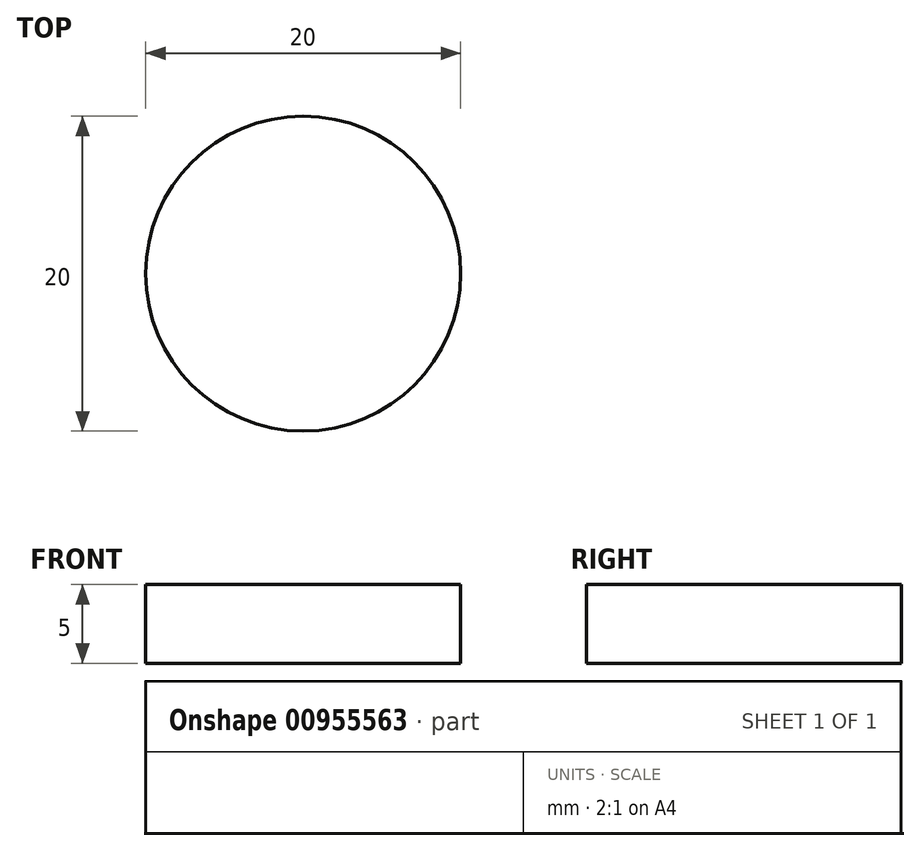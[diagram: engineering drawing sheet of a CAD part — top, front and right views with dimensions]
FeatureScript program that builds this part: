
annotation { "Feature Type Name" : "Feature", "Feature Type Description" : "" }
export const myFeature = defineFeature(function(context is Context, id is Id, definition is map)
    precondition{}
    {
        {
            var Q0;
            Q0=qCreatedBy(makeId("Top.planeOp"),FACE);
            var sketch = newSketch(context, id + "F0", { "sketchPlane" : qUnion([Q0])});
            skCircle(sketch, "E0", {"center": v(0, 0) * mm, "radius": 95 * mm});
            skCircle(sketch, "E1", {"center": v(0, 0) * mm, "radius": 10 * mm});
            skCircle(sketch, "E2", {"center": v(0, 0) * mm, "radius": 20 * mm});
            skCircle(sketch, "E3", {"center": v(0, 0) * mm, "radius": 35 * mm});
            skCircle(sketch, "E4", {"center": v(0, 0) * mm, "radius": 50 * mm});
            skCircle(sketch, "E5", {"center": v(0, 0) * mm, "radius": 65 * mm});
            skCircle(sketch, "E6", {"center": v(0, 0) * mm, "radius": 80 * mm});
            skLineSegment(sketch, "E7", {"start": v(0, 0) * mm, "end": v(0, 95) * mm});
            skLineSegment(sketch, "E8", {"start": v(24.75, 24.75) * mm, "end": v(67.18, 67.18) * mm});
            skLineSegment(sketch, "E9", {"start": v(19.13, 46.2) * mm, "end": v(36.35, 87.77) * mm});
            skLineSegment(sketch, "E10", {"start": v(12.68, 63.75) * mm, "end": v(18.53, 93.17) * mm});
            skLineSegment(sketch, "E11", {"start": v(7.84, 79.61) * mm, "end": v(9.31, 94.54) * mm});
            skLineSegment(sketch, "E12.1.0", {"start": v(-24.75, 24.75) * mm, "end": v(-67.18, 67.18) * mm});
            skLineSegment(sketch, "E12.2.0", {"start": v(-24.75, -24.75) * mm, "end": v(-67.18, -67.18) * mm});
            skLineSegment(sketch, "E12.3.0", {"start": v(24.75, -24.75) * mm, "end": v(67.18, -67.18) * mm});
            skLineSegment(sketch, "E13.1.0", {"start": v(-19.13, 46.2) * mm, "end": v(-36.35, 87.77) * mm});
            skLineSegment(sketch, "E13.2.0", {"start": v(-46.2, 19.13) * mm, "end": v(-87.77, 36.35) * mm});
            skLineSegment(sketch, "E13.3.0", {"start": v(-46.2, -19.13) * mm, "end": v(-87.77, -36.35) * mm});
            skLineSegment(sketch, "E13.4.0", {"start": v(-19.13, -46.2) * mm, "end": v(-36.35, -87.77) * mm});
            skLineSegment(sketch, "E13.5.0", {"start": v(19.13, -46.2) * mm, "end": v(36.35, -87.77) * mm});
            skLineSegment(sketch, "E13.6.0", {"start": v(46.2, -19.13) * mm, "end": v(87.77, -36.35) * mm});
            skLineSegment(sketch, "E13.7.0", {"start": v(46.2, 19.13) * mm, "end": v(87.77, 36.35) * mm});
            skLineSegment(sketch, "E14.1.0", {"start": v(-12.68, 63.75) * mm, "end": v(-18.53, 93.17) * mm});
            skLineSegment(sketch, "E14.2.0", {"start": v(-36.11, 54.05) * mm, "end": v(-52.78, 78.99) * mm});
            skLineSegment(sketch, "E14.3.0", {"start": v(-54.05, 36.11) * mm, "end": v(-78.99, 52.78) * mm});
            skLineSegment(sketch, "E14.4.0", {"start": v(-63.75, 12.68) * mm, "end": v(-93.17, 18.53) * mm});
            skLineSegment(sketch, "E14.5.0", {"start": v(-63.75, -12.68) * mm, "end": v(-93.17, -18.53) * mm});
            skLineSegment(sketch, "E14.6.0", {"start": v(-54.05, -36.11) * mm, "end": v(-78.99, -52.78) * mm});
            skLineSegment(sketch, "E14.7.0", {"start": v(-36.11, -54.05) * mm, "end": v(-52.78, -78.99) * mm});
            skLineSegment(sketch, "E14.8.0", {"start": v(-12.68, -63.75) * mm, "end": v(-18.53, -93.17) * mm});
            skLineSegment(sketch, "E14.9.0", {"start": v(12.68, -63.75) * mm, "end": v(18.53, -93.17) * mm});
            skLineSegment(sketch, "E14.10.0", {"start": v(36.11, -54.05) * mm, "end": v(52.78, -78.99) * mm});
            skLineSegment(sketch, "E14.11.0", {"start": v(54.05, -36.11) * mm, "end": v(78.99, -52.78) * mm});
            skLineSegment(sketch, "E14.12.0", {"start": v(63.75, -12.68) * mm, "end": v(93.17, -18.53) * mm});
            skLineSegment(sketch, "E14.13.0", {"start": v(63.75, 12.68) * mm, "end": v(93.17, 18.53) * mm});
            skLineSegment(sketch, "E14.14.0", {"start": v(54.05, 36.11) * mm, "end": v(78.99, 52.78) * mm});
            skLineSegment(sketch, "E14.15.0", {"start": v(36.11, 54.05) * mm, "end": v(52.78, 78.99) * mm});
            skLineSegment(sketch, "E15.1.0", {"start": v(-7.84, 79.61) * mm, "end": v(-9.31, 94.54) * mm});
            skLineSegment(sketch, "E15.2.0", {"start": v(-23.22, 76.56) * mm, "end": v(-27.58, 90.9) * mm});
            skLineSegment(sketch, "E15.3.0", {"start": v(-37.71, 70.55) * mm, "end": v(-44.78, 83.78) * mm});
            skLineSegment(sketch, "E15.4.0", {"start": v(-50.75, 61.84) * mm, "end": v(-60.27, 73.44) * mm});
            skLineSegment(sketch, "E15.5.0", {"start": v(-61.84, 50.75) * mm, "end": v(-73.44, 60.27) * mm});
            skLineSegment(sketch, "E15.6.0", {"start": v(-70.55, 37.71) * mm, "end": v(-83.78, 44.78) * mm});
            skLineSegment(sketch, "E15.7.0", {"start": v(-76.56, 23.22) * mm, "end": v(-90.9, 27.58) * mm});
            skLineSegment(sketch, "E15.8.0", {"start": v(-79.61, 7.84) * mm, "end": v(-94.54, 9.31) * mm});
            skLineSegment(sketch, "E15.9.0", {"start": v(-79.61, -7.84) * mm, "end": v(-94.54, -9.31) * mm});
            skLineSegment(sketch, "E15.10.0", {"start": v(-76.56, -23.22) * mm, "end": v(-90.9, -27.58) * mm});
            skLineSegment(sketch, "E15.11.0", {"start": v(-70.55, -37.71) * mm, "end": v(-83.78, -44.78) * mm});
            skLineSegment(sketch, "E15.12.0", {"start": v(-61.84, -50.75) * mm, "end": v(-73.44, -60.27) * mm});
            skLineSegment(sketch, "E15.13.0", {"start": v(-50.75, -61.84) * mm, "end": v(-60.27, -73.44) * mm});
            skLineSegment(sketch, "E15.14.0", {"start": v(-37.71, -70.55) * mm, "end": v(-44.78, -83.78) * mm});
            skLineSegment(sketch, "E15.15.0", {"start": v(-23.22, -76.56) * mm, "end": v(-27.58, -90.9) * mm});
            skLineSegment(sketch, "E15.16.0", {"start": v(-7.84, -79.61) * mm, "end": v(-9.31, -94.54) * mm});
            skLineSegment(sketch, "E15.17.0", {"start": v(7.84, -79.61) * mm, "end": v(9.31, -94.54) * mm});
            skLineSegment(sketch, "E15.18.0", {"start": v(23.22, -76.56) * mm, "end": v(27.58, -90.9) * mm});
            skLineSegment(sketch, "E15.19.0", {"start": v(37.71, -70.55) * mm, "end": v(44.78, -83.78) * mm});
            skLineSegment(sketch, "E15.20.0", {"start": v(50.75, -61.84) * mm, "end": v(60.27, -73.44) * mm});
            skLineSegment(sketch, "E15.21.0", {"start": v(61.84, -50.75) * mm, "end": v(73.44, -60.27) * mm});
            skLineSegment(sketch, "E15.22.0", {"start": v(70.55, -37.71) * mm, "end": v(83.78, -44.78) * mm});
            skLineSegment(sketch, "E15.23.0", {"start": v(76.56, -23.22) * mm, "end": v(90.9, -27.58) * mm});
            skLineSegment(sketch, "E15.24.0", {"start": v(79.61, -7.84) * mm, "end": v(94.54, -9.31) * mm});
            skLineSegment(sketch, "E15.25.0", {"start": v(79.61, 7.84) * mm, "end": v(94.54, 9.31) * mm});
            skLineSegment(sketch, "E15.26.0", {"start": v(76.56, 23.22) * mm, "end": v(90.9, 27.58) * mm});
            skLineSegment(sketch, "E15.27.0", {"start": v(70.55, 37.71) * mm, "end": v(83.78, 44.78) * mm});
            skLineSegment(sketch, "E15.28.0", {"start": v(61.84, 50.75) * mm, "end": v(73.44, 60.27) * mm});
            skLineSegment(sketch, "E15.29.0", {"start": v(50.75, 61.84) * mm, "end": v(60.27, 73.44) * mm});
            skLineSegment(sketch, "E15.30.0", {"start": v(37.71, 70.55) * mm, "end": v(44.78, 83.78) * mm});
            skLineSegment(sketch, "E15.31.0", {"start": v(23.22, 76.56) * mm, "end": v(27.58, 90.9) * mm});
            skLineSegment(sketch, "E16.1.0", {"start": v(0, 0) * mm, "end": v(-95, 0) * mm});
            skLineSegment(sketch, "E16.2.0", {"start": v(0, 0) * mm, "end": v(0, -95) * mm});
            skLineSegment(sketch, "E16.3.0", {"start": v(0, 0) * mm, "end": v(95, 0) * mm});
            skSolve(sketch);
        }
        {
            var Q0;
            {var subQ0=sQuery(id+"F0.wireOp",EDGE,"E7");var subQ1=sQuery(id+"F0.wireOp",EDGE,"E1");var subQ2=makeQuery(id+"F0.imprint","INTERSECT",VERTEX,{"derivedFrom":[subQ1,subQ0]});Q0=makeQuery(id+"F0.imprint","IMPRINT",FACE,{"disambiguationData":[TD([[makeQuery(id+"F0.imprint","IMPRINT",EDGE,{"disambiguationData":[TD([[subQ2,-1.0]])],"derivedFrom":subQ1}),1.0]])]});}
            var Q1;
            {var subQ0=sQuery(id+"F0.wireOp",EDGE,"E7");var subQ1=sQuery(id+"F0.wireOp",EDGE,"E1");var subQ2=makeQuery(id+"F0.imprint","INTERSECT",VERTEX,{"derivedFrom":[subQ1,subQ0]});Q1=makeQuery(id+"F0.imprint","IMPRINT",FACE,{"disambiguationData":[TD([[makeQuery(id+"F0.imprint","IMPRINT",EDGE,{"disambiguationData":[TD([[subQ2,1.0]])],"derivedFrom":subQ1}),1.0]])]});}
            var Q2;
            {var subQ0=sQuery(id+"F0.wireOp",EDGE,"E16.3.0");var subQ1=sQuery(id+"F0.wireOp",EDGE,"E1");var subQ2=makeQuery(id+"F0.imprint","INTERSECT",VERTEX,{"derivedFrom":[subQ1,subQ0]});Q2=makeQuery(id+"F0.imprint","IMPRINT",FACE,{"disambiguationData":[TD([[makeQuery(id+"F0.imprint","IMPRINT",EDGE,{"disambiguationData":[TD([[subQ2,1.0]])],"derivedFrom":subQ1}),1.0]])]});}
            var Q3;
            {var subQ0=sQuery(id+"F0.wireOp",EDGE,"E16.1.0");var subQ1=sQuery(id+"F0.wireOp",EDGE,"E1");var subQ2=makeQuery(id+"F0.imprint","INTERSECT",VERTEX,{"derivedFrom":[subQ1,subQ0]});Q3=makeQuery(id+"F0.imprint","IMPRINT",FACE,{"disambiguationData":[TD([[makeQuery(id+"F0.imprint","IMPRINT",EDGE,{"disambiguationData":[TD([[subQ2,-1.0]])],"derivedFrom":subQ1}),1.0]])]});}
            extrude(context, id + "F1", {"entities" : qUnion([Q0, Q1, Q2, Q3]), "depth" : 5 * mm, "offsetDistance" : 25 * mm});
        }
    });
